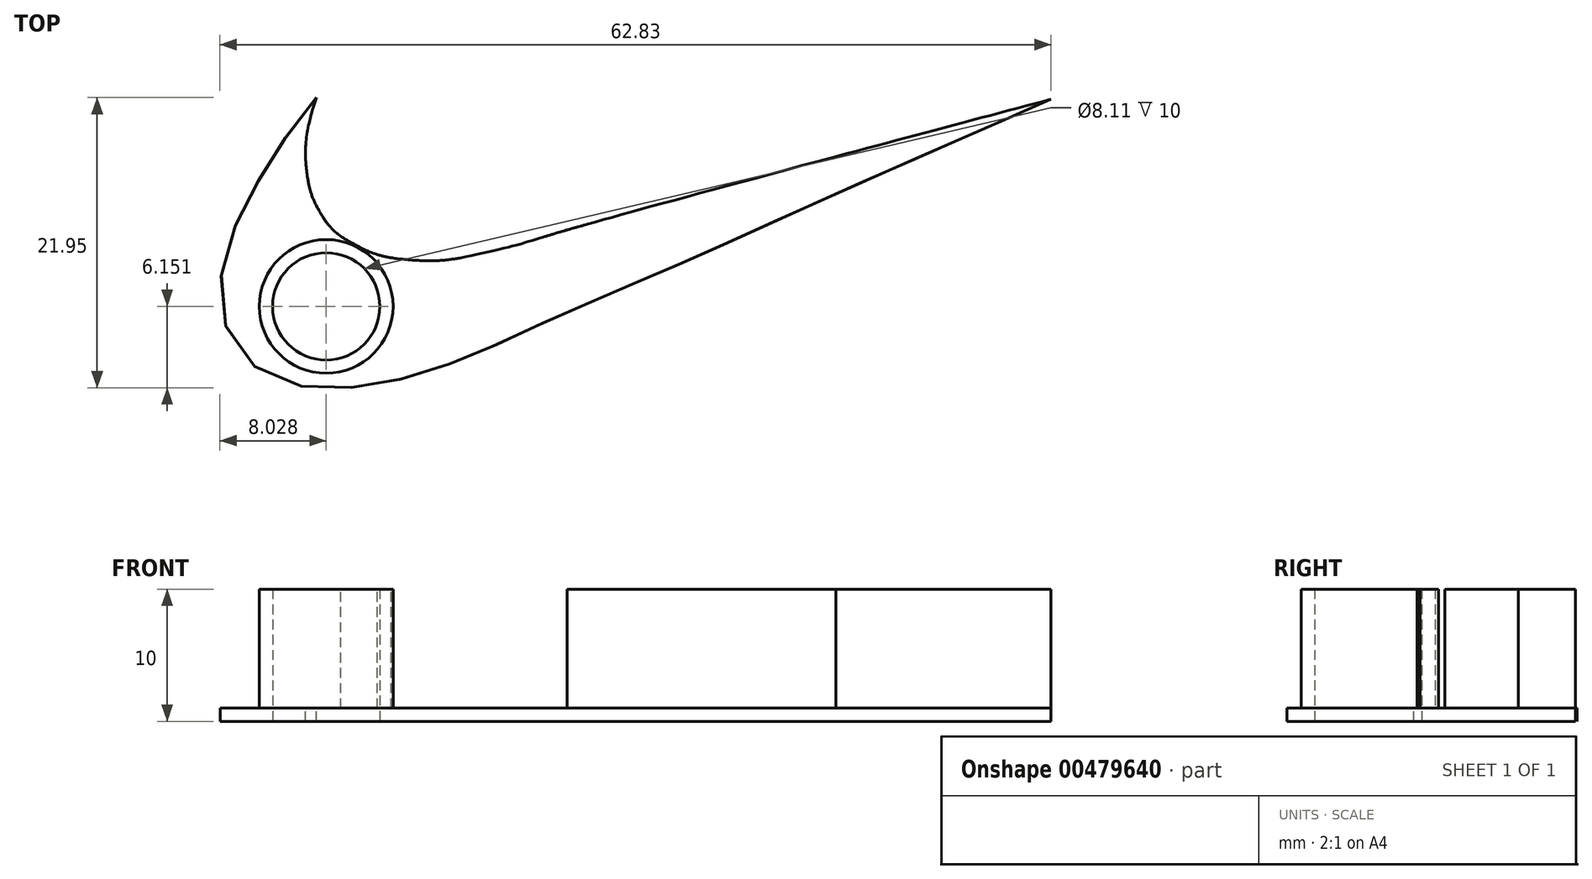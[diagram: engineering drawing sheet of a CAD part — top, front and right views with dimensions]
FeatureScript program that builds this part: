
annotation { "Feature Type Name" : "Feature", "Feature Type Description" : "" }
export const myFeature = defineFeature(function(context is Context, id is Id, definition is map)
    precondition{}
    {
        {
            var Q0;
            Q0=qCreatedBy(makeId("Top.planeOp"),FACE);
            var sketch = newSketch(context, id + "F0", { "sketchPlane" : qUnion([Q0])});
            skFitSpline(sketch, "E0", {"points": [v(50.7, 13.66) * mm, v(45.55, 11.28) * mm, v(42.32, 9.8) * mm, v(23.15, 1.38) * mm, v(10.84, -4.15) * mm, v(0, -8.83) * mm, v(-4.75, -11.01) * mm, v(-9.74, -12.8) * mm, v(-14.5, -13.74) * mm, v(-17.6, -13.7) * mm, v(-19, -13.6) * mm, v(-20.75, -13.06) * mm, v(-22.14, -12.34) * mm, v(-23.17, -11.6) * mm, v(-24.15, -10.52) * mm, v(-24.98, -9.15) * mm, v(-25.5, -7.32) * mm, v(-25.7, -5.93) * mm, v(-25.7, -5.39) * mm, v(-25.68, -4.67) * mm, v(-25.53, -3.74) * mm, v(-25.27, -2.37) * mm, v(-24.84, -1.15) * mm, v(-24.27, 0.39) * mm, v(-23.52, 1.82) * mm, v(-22.91, 2.94) * mm, v(-21.39, 5.51) * mm, v(-19.47, 8.24) * mm, v(-17.38, 10.8) * mm, v(-14.55, 13.8) * mm, v(-14.42, 13.74) * mm, v(-14.55, 13.42) * mm, v(-15.13, 12.25) * mm, v(-15.83, 10.7) * mm, v(-16.45, 8.95) * mm, v(-17.13, 6.43) * mm, v(-17.24, 4.57) * mm, v(-17.08, 3.15) * mm, v(-16.8, 2.06) * mm, v(-16.42, 1.25) * mm, v(-15.58, 0) * mm, v(-14.31, -0.92) * mm, v(-12.58, -1.73) * mm, v(-10.33, -2.1) * mm, v(-7.88, -2.13) * mm, v(-5.06, -1.61) * mm, v(-2.23, -0.92) * mm, v(0.83, 0) * mm, v(37.8, 10) * mm, v(49.42, 13.21) * mm, v(50.7, 13.66) * mm]});
            skCircle(sketch, "E1", {"center": v(-16.68, -6.62) * mm, "radius": 4.06 * mm});
            skSolve(sketch);
        }
        {
            var Q0;
            Q0=makeQuery(id+"F0.imprint","IMPRINT",FACE,{"disambiguationData":[TD([[makeQuery(id+"F0.imprint","IMPRINT",EDGE,{"derivedFrom":sQuery(id+"F0.wireOp",EDGE,"E0")}),-1.0]])]});
            extrude(context, id + "F1", {"entities" : qUnion([Q0]), "depth" : 10 * mm});
        }
        {
            var Q0;
            Q0=makeQuery(id+"F1.opExtrude","CAP_FACE",FACE,{"disambiguationData":[OSD([sQuery(id+"F0.wireOp",EDGE,"E0")])],"isStart":false});
            shell(context, id + "F2", {"entities" : qUnion([Q0]), "thickness" : 1 * mm});
        }
        {
            var Q0;
            {var subQ0=sQuery(id+"F0.wireOp",EDGE,"E1");var subQ1=sQuery(id+"F0.wireOp",EDGE,"E0");Q0=makeQuery(id+"F2.opShell","OFFSET_FACE",FACE,{"disambiguationData":[OSD([subQ1,subQ0]),TDD([makeQuery(id+"F1.opExtrude","CAP_FACE",FACE,{"disambiguationData":[OSD([subQ1,subQ0])],"isStart":false})])]});}
            extrude(context, id + "F3", {"entities" : qUnion([Q0]), "operationType" : NewBodyOperationType.REMOVE, "oppositeDirection" : true, "depth" : 25 * mm});
        }
    });
